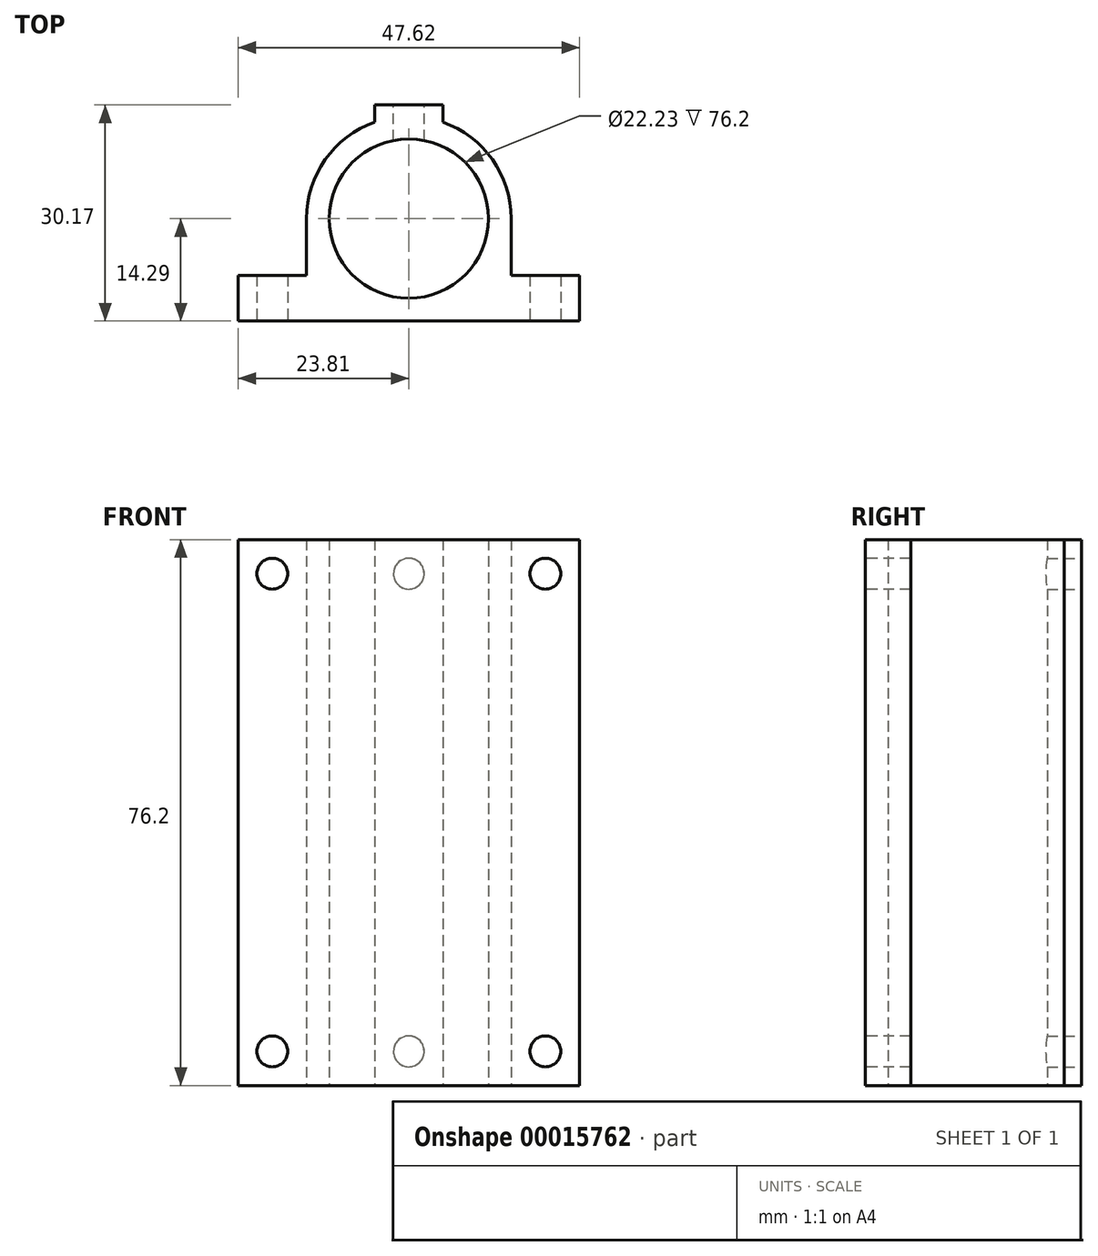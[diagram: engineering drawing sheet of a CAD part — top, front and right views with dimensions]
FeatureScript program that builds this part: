
annotation { "Feature Type Name" : "Feature", "Feature Type Description" : "" }
export const myFeature = defineFeature(function(context is Context, id is Id, definition is map)
    precondition{}
    {
        {
            var Q0;
            Q0=qCreatedBy(makeId("Top.planeOp"),FACE);
            var sketch = newSketch(context, id + "F0", { "sketchPlane" : qUnion([Q0])});
            skCircle(sketch, "E0", {"center": v(0, 0) * mm, "radius": 11.11 * mm});
            skLineSegment(sketch, "E1", {"start": v(0, 0) * mm, "end": v(0, 13.47) * mm, "construction": true});
            skLineSegment(sketch, "E2", {"start": v(-4.76, 13.47) * mm, "end": v(4.76, 13.47) * mm, "construction": true});
            skArc(sketch, "E3", {"start": v(-4.76, 13.47) * mm, "mid": v(-11.67, 8.25) * mm, "end": v(-14.29, 0) * mm});
            skArc(sketch, "E4", {"start": v(14.29, 0) * mm, "mid": v(11.67, 8.25) * mm, "end": v(4.76, 13.47) * mm});
            skLineSegment(sketch, "E5.top", {"start": v(-4.76, 15.88) * mm, "end": v(4.76, 15.88) * mm});
            skLineSegment(sketch, "E5.left", {"start": v(-4.76, 13.47) * mm, "end": v(-4.76, 15.88) * mm});
            skLineSegment(sketch, "E5.right", {"start": v(4.76, 13.47) * mm, "end": v(4.76, 15.88) * mm});
            skLineSegment(sketch, "E6.bottom", {"start": v(23.81, -14.29) * mm, "end": v(-23.81, -14.29) * mm});
            skLineSegment(sketch, "E6.left", {"start": v(23.81, -14.29) * mm, "end": v(23.81, -7.94) * mm});
            skLineSegment(sketch, "E6.right", {"start": v(-23.81, -14.29) * mm, "end": v(-23.81, -7.94) * mm});
            skLineSegment(sketch, "E7.bottom", {"start": v(14.29, 0) * mm, "end": v(-14.29, 0) * mm, "construction": true});
            skLineSegment(sketch, "E7.left", {"start": v(14.29, 0) * mm, "end": v(14.29, -7.94) * mm});
            skLineSegment(sketch, "E7.right", {"start": v(-14.29, 0) * mm, "end": v(-14.29, -7.94) * mm});
            skLineSegment(sketch, "E8", {"start": v(-23.81, -7.94) * mm, "end": v(-14.29, -7.94) * mm});
            skLineSegment(sketch, "E9", {"start": v(14.29, -7.94) * mm, "end": v(23.81, -7.94) * mm});
            skLineSegment(sketch, "E10", {"start": v(0, 0) * mm, "end": v(0, -14.29) * mm, "construction": true});
            skSolve(sketch);
        }
        {
            var Q0;
            Q0=qSketchRegion(id+"F0",true);
            extrude(context, id + "F1", {"entities" : qUnion([Q0]), "depth" : 76.2 * mm});
        }
        {
            var Q0;
            Q0=makeQuery(id+"F1.opExtrude","SWEPT_FACE",FACE,{"disambiguationData":[OSD([sQuery(id+"F0.wireOp",EDGE,"E5.top")])]});
            var sketch = newSketch(context, id + "F2", { "sketchPlane" : qUnion([Q0])});
            skLineSegment(sketch, "E11.bottom", {"start": v(0, 0) * mm, "end": v(4.76, 0) * mm, "construction": true});
            skLineSegment(sketch, "E11.top", {"start": v(0, 4.76) * mm, "end": v(4.76, 4.76) * mm, "construction": true});
            skLineSegment(sketch, "E11.left", {"start": v(0, 0) * mm, "end": v(0, 4.76) * mm, "construction": true});
            skLineSegment(sketch, "E11.right", {"start": v(4.76, 0) * mm, "end": v(4.76, 4.76) * mm, "construction": true});
            skLineSegment(sketch, "E12.left", {"start": v(0, 4.76) * mm, "end": v(0, 71.44) * mm, "construction": true});
            skCircle(sketch, "E13", {"center": v(0, 4.76) * mm, "radius": 2.15 * mm});
            skCircle(sketch, "E14", {"center": v(0, 71.44) * mm, "radius": 2.15 * mm});
            skLineSegment(sketch, "E15.bottom", {"start": v(0, 71.44) * mm, "end": v(-4.76, 71.44) * mm, "construction": true});
            skLineSegment(sketch, "E15.top", {"start": v(0, 76.2) * mm, "end": v(-4.76, 76.2) * mm, "construction": true});
            skLineSegment(sketch, "E15.left", {"start": v(0, 71.44) * mm, "end": v(0, 76.2) * mm, "construction": true});
            skLineSegment(sketch, "E15.right", {"start": v(-4.76, 71.44) * mm, "end": v(-4.76, 76.2) * mm, "construction": true});
            skSolve(sketch);
        }
        {
            var Q0;
            Q0=qSketchRegion(id+"F2",true);
            var Q1;
            Q1=makeQuery(id+"F1.opExtrude","SWEPT_FACE",FACE,{"disambiguationData":[OSD([sQuery(id+"F0.wireOp",EDGE,"djldysEu-ljvw-hPGd-3HMA-uMFqrL7TPg54")])]});
            extrude(context, id + "F3", {"entities" : qUnion([Q0]), "operationType" : NewBodyOperationType.REMOVE, "oppositeDirection" : true, "endBoundEntityFace" : qUnion([Q1]), "depth" : 6.35 * mm});
        }
        {
            var Q0;
            Q0=makeQuery(id+"F1.opExtrude","SWEPT_FACE",FACE,{"disambiguationData":[OSD([sQuery(id+"F0.wireOp",EDGE,"E6.bottom")])]});
            var sketch = newSketch(context, id + "F4", { "sketchPlane" : qUnion([Q0])});
            skLineSegment(sketch, "E16", {"start": v(0, 76.2) * mm, "end": v(0, 0) * mm, "construction": true});
            skLineSegment(sketch, "E17.bottom", {"start": v(-23.81, 76.2) * mm, "end": v(-19.05, 76.2) * mm, "construction": true});
            skLineSegment(sketch, "E17.top", {"start": v(-23.81, 71.44) * mm, "end": v(-19.05, 71.44) * mm, "construction": true});
            skLineSegment(sketch, "E17.left", {"start": v(-23.81, 76.2) * mm, "end": v(-23.81, 71.44) * mm, "construction": true});
            skLineSegment(sketch, "E17.right", {"start": v(-19.05, 76.2) * mm, "end": v(-19.05, 71.44) * mm, "construction": true});
            skLineSegment(sketch, "E18.bottom", {"start": v(-19.05, 71.44) * mm, "end": v(19.05, 71.44) * mm, "construction": true});
            skLineSegment(sketch, "E18.top", {"start": v(-19.05, 4.76) * mm, "end": v(19.05, 4.76) * mm, "construction": true});
            skLineSegment(sketch, "E18.left", {"start": v(-19.05, 71.44) * mm, "end": v(-19.05, 4.76) * mm, "construction": true});
            skLineSegment(sketch, "E18.right", {"start": v(19.05, 71.44) * mm, "end": v(19.05, 4.76) * mm, "construction": true});
            skPoint(sketch, "E18.middle", {"position": v(0, 38.1) * mm});
            skCircle(sketch, "E19", {"center": v(-19.05, 71.44) * mm, "radius": 2.15 * mm});
            skCircle(sketch, "E20", {"center": v(19.05, 71.44) * mm, "radius": 2.15 * mm});
            skCircle(sketch, "E21", {"center": v(19.05, 4.76) * mm, "radius": 2.15 * mm});
            skCircle(sketch, "E22", {"center": v(-19.05, 4.76) * mm, "radius": 2.15 * mm});
            skSolve(sketch);
        }
        {
            var Q0;
            Q0 = qSketchRegion(id + "F4", true);
            var Q1;
            Q1=makeQuery(id+"F1.opExtrude","SWEPT_FACE",FACE,{"disambiguationData":[OSD([sQuery(id+"F0.wireOp",EDGE,"E9")])]});
            extrude(context, id + "F5", {"entities" : qUnion([Q0]), "operationType" : NewBodyOperationType.REMOVE, "endBound" : BoundingType.UP_TO_SURFACE, "oppositeDirection" : true, "endBoundEntityFace" : qUnion([Q1]), "depth" : 25.4 * mm});
        }
    });
